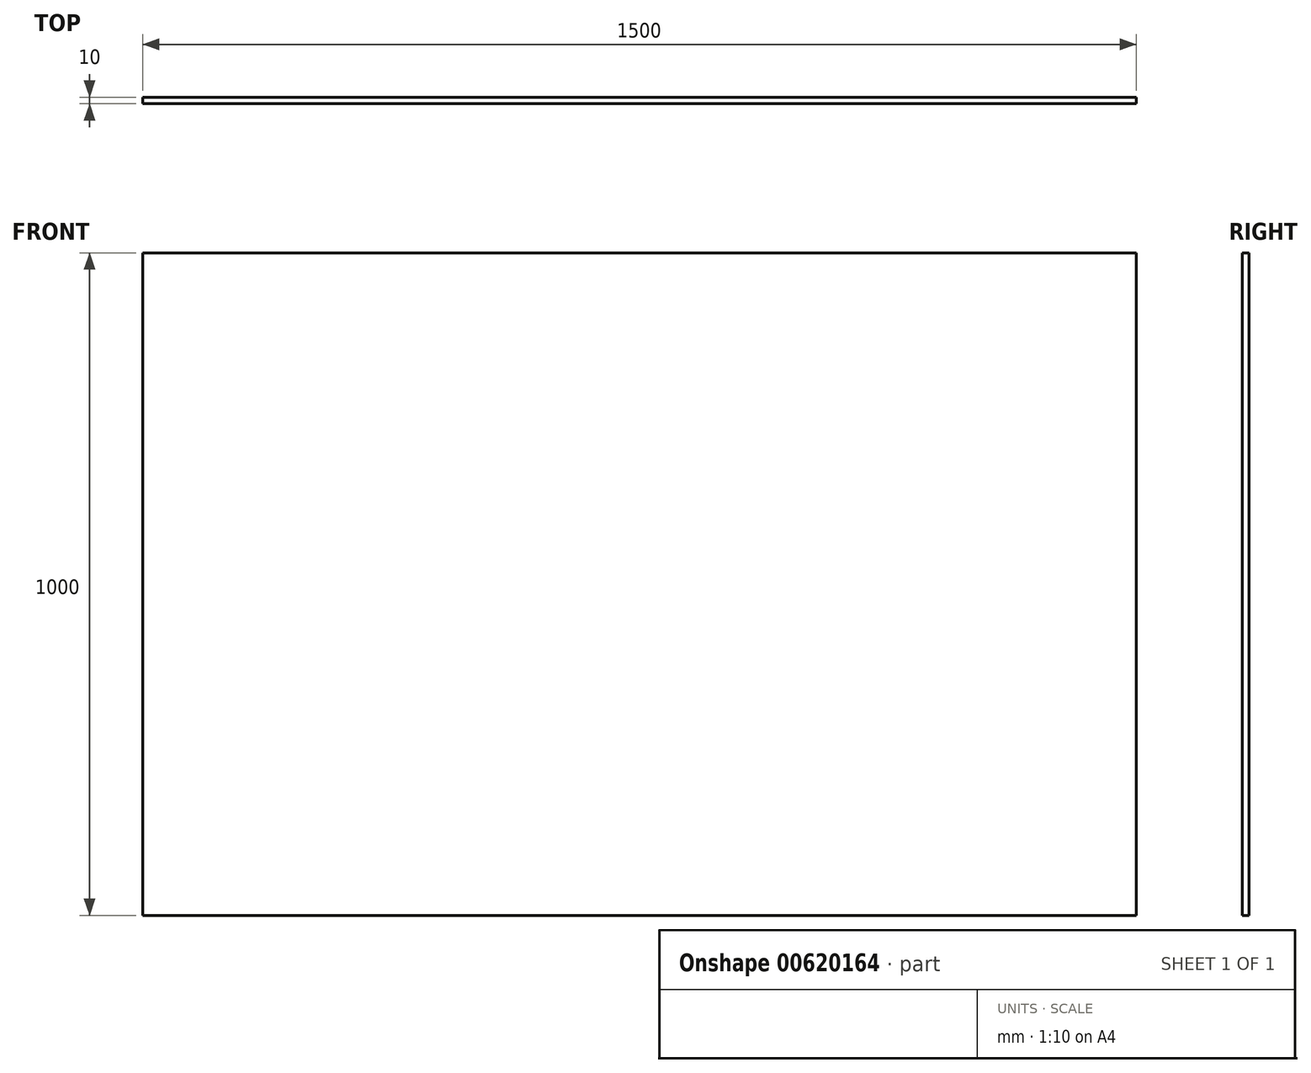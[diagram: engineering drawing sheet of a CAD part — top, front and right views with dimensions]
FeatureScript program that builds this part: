
annotation { "Feature Type Name" : "Feature", "Feature Type Description" : "" }
export const myFeature = defineFeature(function(context is Context, id is Id, definition is map)
    precondition{}
    {
        {
            var Q0;
            Q0=qCreatedBy(makeId("Front.planeOp"),FACE);
            var sketch = newSketch(context, id + "F0", { "sketchPlane" : qUnion([Q0])});
            skLineSegment(sketch, "E0.bottom", {"start": v(750, 500) * mm, "end": v(-750, 500) * mm});
            skLineSegment(sketch, "E0.top", {"start": v(750, -500) * mm, "end": v(-750, -500) * mm});
            skLineSegment(sketch, "E0.left", {"start": v(750, 500) * mm, "end": v(750, -500) * mm});
            skLineSegment(sketch, "E0.right", {"start": v(-750, 500) * mm, "end": v(-750, -500) * mm});
            skPoint(sketch, "E0.middle", {"position": v(0, 0) * mm});
            skSolve(sketch);
        }
        {
            var Q0;
            Q0=makeQuery(id+"F0.imprint","IMPRINT",FACE,{"disambiguationData":[TD([[makeQuery(id+"F0.imprint","IMPRINT",EDGE,{"derivedFrom":sQuery(id+"F0.wireOp",EDGE,"E0.bottom")}),1.0]])]});
            extrude(context, id + "F1", {"entities" : qUnion([Q0]), "depth" : 10 * mm, "offsetDistance" : 25 * mm});
        }
    });
